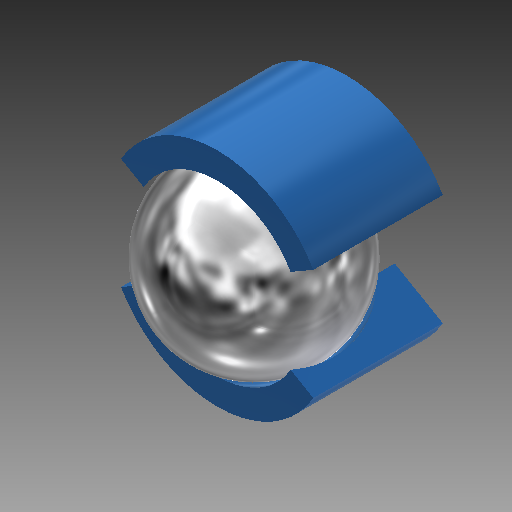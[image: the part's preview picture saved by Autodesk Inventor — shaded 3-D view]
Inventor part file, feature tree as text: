
AUTODESK INVENTOR PART (.ipt)
format: ipt  version: 2017 (Build 210142000, 142)  size: 219,648 bytes
history: native  units: mm
features: sketch x3, revolve x2, extrude x1, boolean_combine x1
ambient origin geometry x8: Origin, YZ Plane, XZ Plane, XY Plane, X Axis, Y Axis, Z Axis, Center Point
bodies: Solid2 (feature_tree), Solid3 (feature_tree), Solid1 (feature_tree)
feature tree (7):
  extrude  "Extrusion1"  Depth=3.0mm
  revolve  "Revolution1"  [1 undecoded]
  boolean_combine  "Combine1"
  revolve  "Revolution2"  [1 undecoded]
  sketch  "Sketch1"  dims[d0=6.0mm d1=3.0mm]
  sketch  "Sketch4"  dims[d2=1.0mm d3=2.5mm d4=0.0mm d5=0.0mm d8=2.5mm]
  sketch  "Sketch5"  dims[d9=20.071286mm d10=2.4mm d11=20.071286mm]
note: 2 required parameter values undecoded (feature->parameter linkage not recoverable at this tier; creation-order binding heuristic only, values carry confidence <= 0.55)
